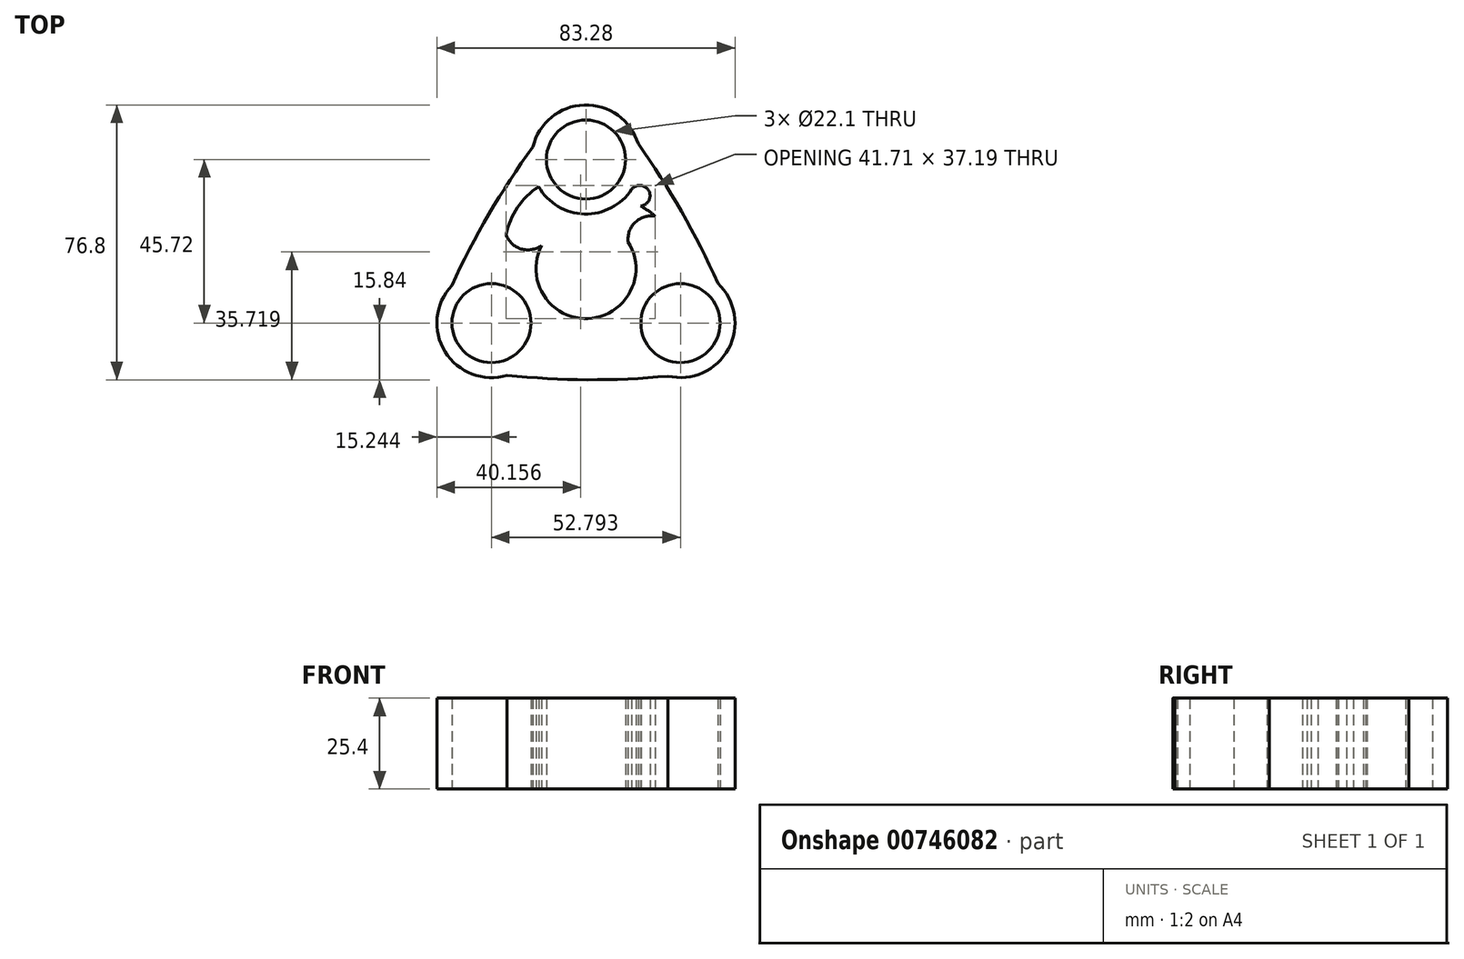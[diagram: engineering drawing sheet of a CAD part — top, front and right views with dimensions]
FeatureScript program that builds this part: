
annotation { "Feature Type Name" : "Feature", "Feature Type Description" : "" }
export const myFeature = defineFeature(function(context is Context, id is Id, definition is map)
    precondition{}
    {
        {
            var Q0;
            Q0=qCreatedBy(makeId("Top.planeOp"),FACE);
            var sketch = newSketch(context, id + "F0", { "sketchPlane" : qUnion([Q0])});
            skCircle(sketch, "E0", {"center": v(0, 0) * mm, "radius": 13.97 * mm});
            skCircle(sketch, "E1", {"center": v(0, 0) * mm, "radius": 11.05 * mm});
            skLineSegment(sketch, "E2", {"start": v(0, 0) * mm, "end": v(0, 30.48) * mm});
            skCircle(sketch, "E3", {"center": v(0, 30.48) * mm, "radius": 15.24 * mm});
            skCircle(sketch, "E4", {"center": v(0, 30.48) * mm, "radius": 11.05 * mm});
            skCircle(sketch, "E5.1.0", {"center": v(-26.4, -15.24) * mm, "radius": 15.24 * mm});
            skCircle(sketch, "E5.1.1", {"center": v(-26.4, -15.24) * mm, "radius": 11.05 * mm});
            skCircle(sketch, "E5.2.0", {"center": v(26.4, -15.24) * mm, "radius": 15.24 * mm});
            skCircle(sketch, "E5.2.1", {"center": v(26.4, -15.24) * mm, "radius": 11.05 * mm});
            skArc(sketch, "E6", {"start": v(36.84, -4.14) * mm, "mid": v(24.05, 20.44) * mm, "end": v(8.31, 43.25) * mm});
            skArc(sketch, "E7", {"start": v(26.4, 0) * mm, "mid": v(22.35, 11.33) * mm, "end": v(12.75, 18.59) * mm});
            skArc(sketch, "E8", {"start": v(12.75, 18.59) * mm, "mid": v(17.91, 20.36) * mm, "end": v(12.75, 22.14) * mm});
            skArc(sketch, "E9", {"start": v(19.37, 14.6) * mm, "mid": v(13.81, 12.94) * mm, "end": v(11.78, 7.5) * mm});
            skArc(sketch, "E10.1.0", {"start": v(-14.83, 33.97) * mm, "mid": v(-29.73, 10.6) * mm, "end": v(-41.61, -14.43) * mm});
            skArc(sketch, "E10.1.1", {"start": v(-13.2, 22.86) * mm, "mid": v(-21, 13.7) * mm, "end": v(-22.47, 1.75) * mm});
            skArc(sketch, "E10.1.2", {"start": v(-22.34, 9.47) * mm, "mid": v(-18.11, 5.5) * mm, "end": v(-12.4, 6.45) * mm});
            skArc(sketch, "E10.2.0", {"start": v(-22, -29.83) * mm, "mid": v(5.68, -31.05) * mm, "end": v(33.3, -28.83) * mm});
            skSolve(sketch);
        }
        {
            var Q0;
            Q0 = qSketchRegion(id + "F0", true);
            extrude(context, id + "F1", {"entities" : qUnion([Q0]), "depth" : 25.4 * mm, "offsetDistance" : 25.4 * mm});
        }
        {
            var Q0;
            Q0 = qSketchRegion(id + "F0", true);
            extrude(context, id + "F2", {"entities" : qUnion([Q0]), "operationType" : NewBodyOperationType.ADD, "depth" : 25.4 * mm, "offsetDistance" : 25.4 * mm});
        }
    });
